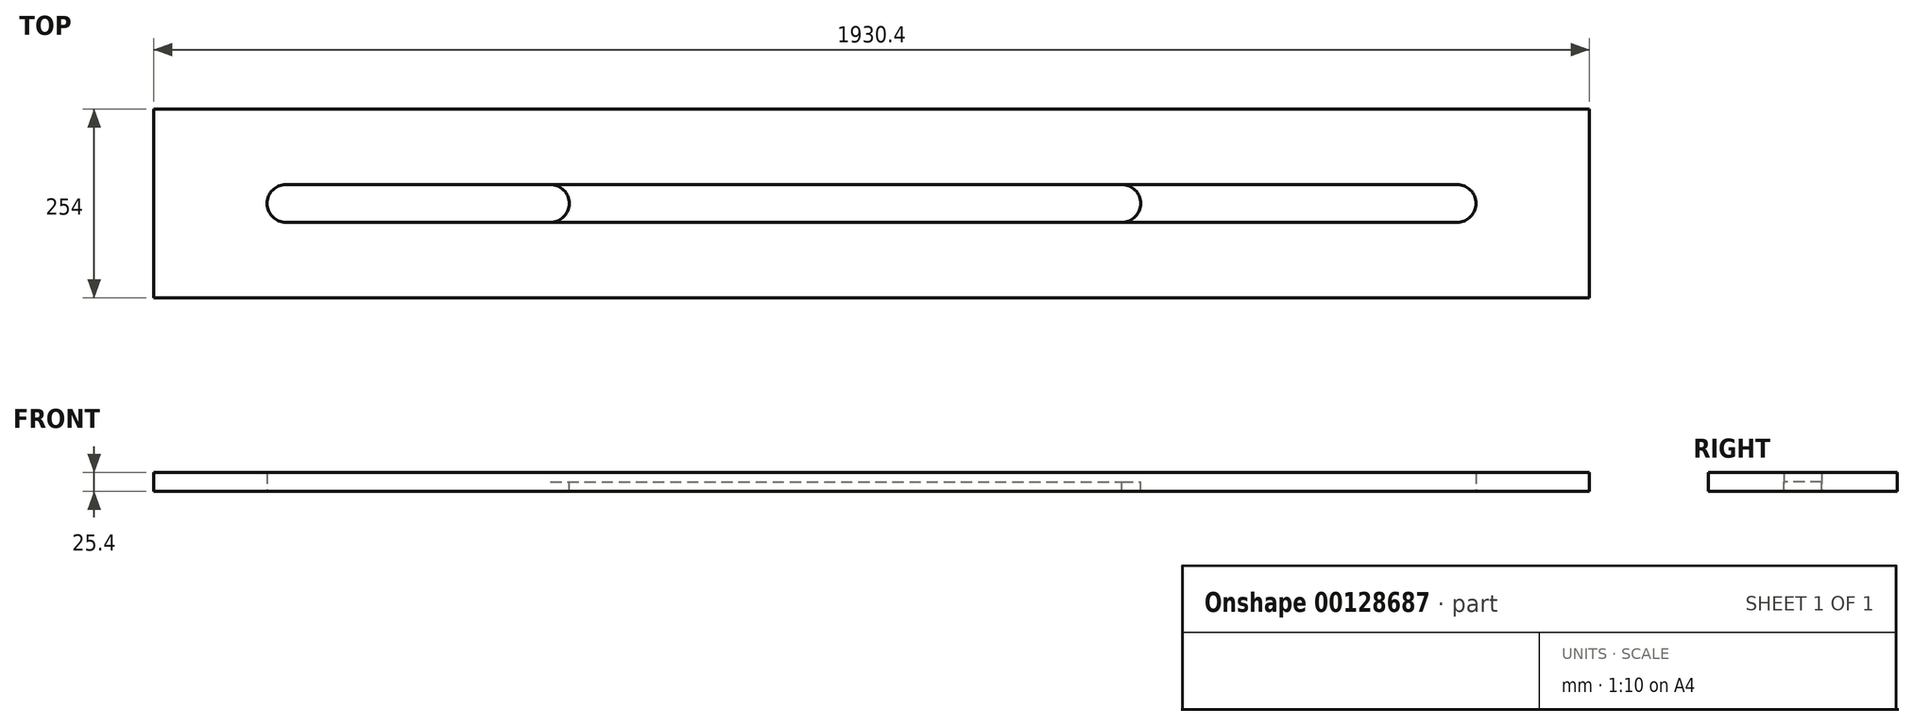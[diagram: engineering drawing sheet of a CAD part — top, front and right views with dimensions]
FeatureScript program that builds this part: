
annotation { "Feature Type Name" : "Feature", "Feature Type Description" : "" }
export const myFeature = defineFeature(function(context is Context, id is Id, definition is map)
    precondition{}
    {
        {
            var Q0;
            Q0=qCreatedBy(makeId("Top.planeOp"),FACE);
            var sketch = newSketch(context, id + "F0", { "sketchPlane" : qUnion([Q0])});
            skLineSegment(sketch, "E0.bottom", {"start": v(-1040.3, -260.9) * mm, "end": v(890.1, -260.9) * mm});
            skLineSegment(sketch, "E0.top", {"start": v(-1040.3, -6.9) * mm, "end": v(890.1, -6.9) * mm});
            skLineSegment(sketch, "E0.left", {"start": v(-1040.3, -260.9) * mm, "end": v(-1040.3, -6.9) * mm});
            skLineSegment(sketch, "E0.right", {"start": v(890.1, -260.9) * mm, "end": v(890.1, -6.9) * mm});
            skArc(sketch, "E1", {"start": v(-862.5, -108.5) * mm, "mid": v(-887.9, -133.9) * mm, "end": v(-862.5, -159.3) * mm});
            skArc(sketch, "E2", {"start": v(712.3, -159.3) * mm, "mid": v(737.7, -133.9) * mm, "end": v(712.3, -108.5) * mm});
            skLineSegment(sketch, "E3", {"start": v(-862.5, -108.5) * mm, "end": v(712.3, -108.5) * mm});
            skLineSegment(sketch, "E4", {"start": v(-862.5, -159.3) * mm, "end": v(712.3, -159.3) * mm});
            skSolve(sketch);
        }
        {
            var Q0;
            Q0=makeQuery(id+"F0.imprint","IMPRINT",FACE,{"disambiguationData":[TD([[makeQuery(id+"F0.imprint","IMPRINT",EDGE,{"derivedFrom":sQuery(id+"F0.wireOp",EDGE,"E0.bottom")}),1.0]])]});
            extrude(context, id + "F1", {"entities" : qUnion([Q0]), "depth" : 12.7 * mm});
        }
        {
            var Q0;
            Q0=makeQuery(id+"F1.opExtrude","CAP_FACE",FACE,{"disambiguationData":[OSD([sQuery(id+"F0.wireOp",EDGE,"E0.bottom"),sQuery(id+"F0.wireOp",EDGE,"E0.top"),sQuery(id+"F0.wireOp",EDGE,"E0.left"),sQuery(id+"F0.wireOp",EDGE,"E0.right"),sQuery(id+"F0.wireOp",EDGE,"E1"),sQuery(id+"F0.wireOp",EDGE,"E2"),sQuery(id+"F0.wireOp",EDGE,"E3"),sQuery(id+"F0.wireOp",EDGE,"E4")])],"isStart":true});
            var sketch = newSketch(context, id + "F2", { "sketchPlane" : qUnion([Q0])});
            skArc(sketch, "E5", {"start": v(-506.9, 108.5) * mm, "mid": v(-481.5, 133.9) * mm, "end": v(-506.9, 159.3) * mm});
            skArc(sketch, "E6", {"start": v(-411.65, 159.3) * mm, "mid": v(-437.05, 133.9) * mm, "end": v(-411.65, 108.5) * mm});
            skLineSegment(sketch, "E7", {"start": v(-1040.3, 260.9) * mm, "end": v(-1040.3, 6.9) * mm});
            skLineSegment(sketch, "E8", {"start": v(-1040.3, 6.9) * mm, "end": v(890.1, 6.9) * mm});
            skLineSegment(sketch, "E9", {"start": v(890.1, 6.9) * mm, "end": v(890.1, 260.9) * mm});
            skLineSegment(sketch, "E10", {"start": v(890.1, 260.9) * mm, "end": v(-1040.3, 260.9) * mm});
            skLineSegment(sketch, "E11", {"start": v(-862.5, 159.3) * mm, "end": v(-506.9, 159.3) * mm});
            skLineSegment(sketch, "E12", {"start": v(-862.5, 108.5) * mm, "end": v(-506.9, 108.5) * mm});
            skArc(sketch, "E13", {"start": v(-862.5, 159.3) * mm, "mid": v(-887.9, 133.9) * mm, "end": v(-862.5, 108.5) * mm});
            skArc(sketch, "E14.MirrorCS", {"start": v(261.45, 159.3) * mm, "mid": v(286.85, 133.9) * mm, "end": v(261.45, 108.5) * mm});
            skArc(sketch, "E15.MirrorCS", {"start": v(712.3, 159.3) * mm, "mid": v(737.7, 133.9) * mm, "end": v(712.3, 108.5) * mm});
            skLineSegment(sketch, "E16.MirrorCS", {"start": v(712.3, 159.3) * mm, "end": v(356.7, 159.3) * mm});
            skArc(sketch, "E17.MirrorCS", {"start": v(356.7, 108.5) * mm, "mid": v(331.3, 133.9) * mm, "end": v(356.7, 159.3) * mm});
            skLineSegment(sketch, "E18.MirrorCS", {"start": v(712.3, 108.5) * mm, "end": v(356.7, 108.5) * mm});
            skLineSegment(sketch, "E19", {"start": v(-411.65, 159.3) * mm, "end": v(261.45, 159.3) * mm});
            skLineSegment(sketch, "E20", {"start": v(-411.65, 108.5) * mm, "end": v(261.45, 108.5) * mm});
            skSolve(sketch);
        }
        {
            var Q0;
            {var subQ0=sQuery(id+"F2.wireOp",EDGE,"E5");Q0=makeQuery(id+"F2.imprint","IMPRINT",FACE,{"disambiguationData":[TD([[makeQuery(id+"F2.imprint","IMPRINT",EDGE,{"derivedFrom":subQ0}),-1.0]])]});}
            var Q1;
            {var subQ0=sQuery(id+"F2.wireOp",EDGE,"78cc1cad-d53e-4137-8bde-8594e97f79ef0.MirrorCS");Q1=makeQuery(id+"F2.imprint","IMPRINT",FACE,{"disambiguationData":[TD([[makeQuery(id+"F2.imprint","IMPRINT",EDGE,{"derivedFrom":subQ0}),1.0]])]});}
            var Q2;
            {var subQ0=sQuery(id+"F2.wireOp",EDGE,"E14.MirrorCS");Q2=makeQuery(id+"F2.imprint","IMPRINT",FACE,{"disambiguationData":[TD([[makeQuery(id+"F2.imprint","IMPRINT",EDGE,{"derivedFrom":subQ0}),1.0]])]});}
            var Q3;
            Q3=makeQuery(id+"F0.imprint","IMPRINT",FACE,{"disambiguationData":[TD([[makeQuery(id+"F0.imprint","IMPRINT",EDGE,{"derivedFrom":sQuery(id+"F0.wireOp",EDGE,"E0.bottom")}),1.0]])]});
            extrude(context, id + "F3", {"entities" : qUnion([Q0, Q1, Q2, Q3]), "operationType" : NewBodyOperationType.ADD, "depth" : 12.7 * mm});
        }
    });
